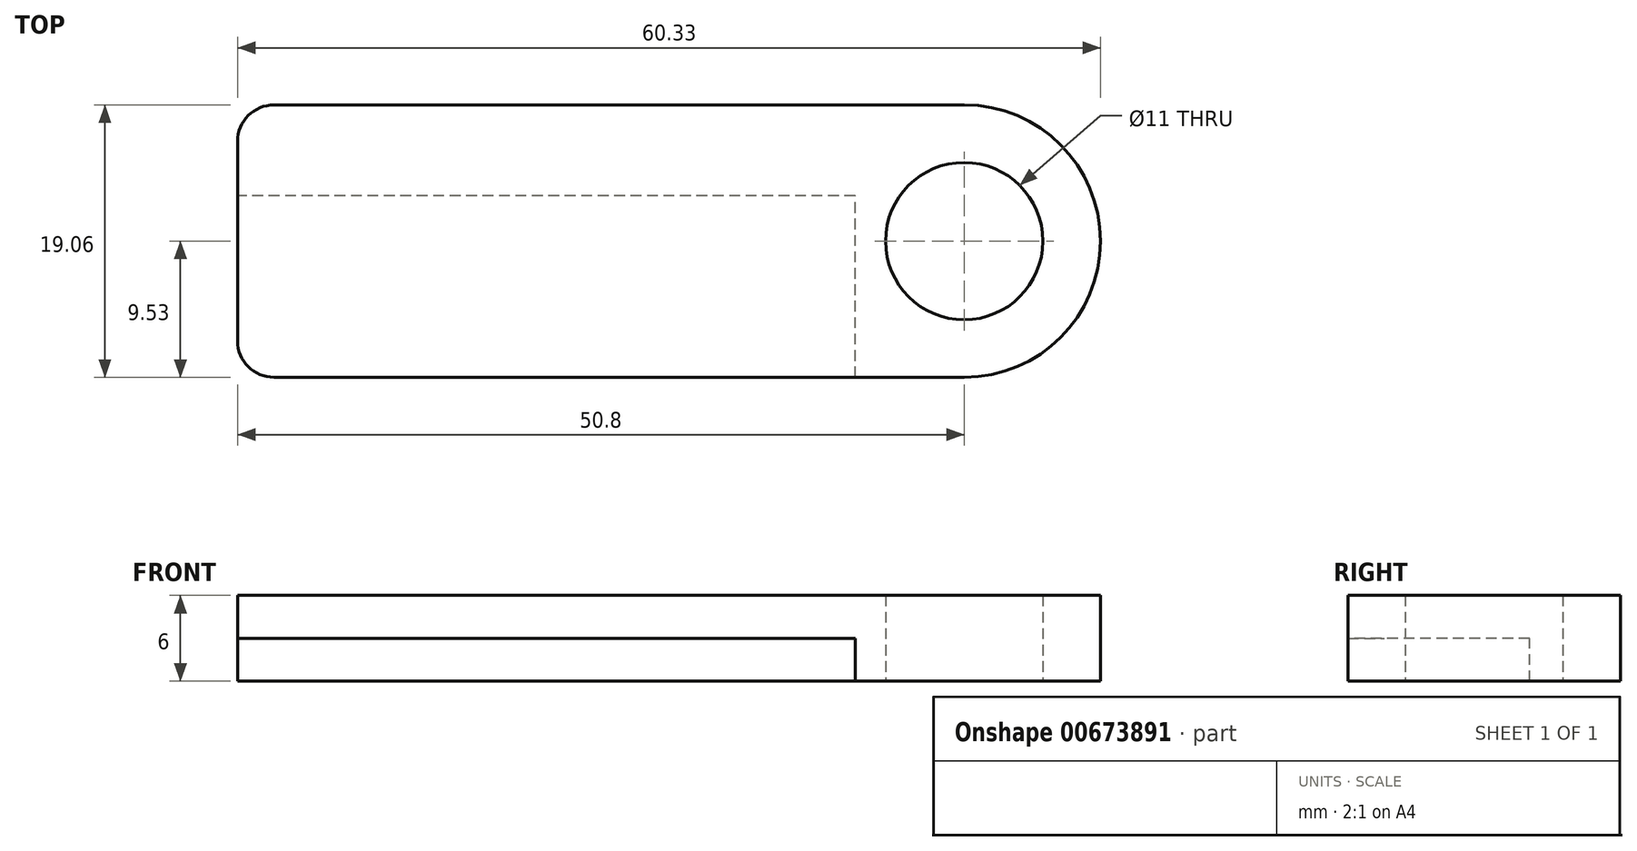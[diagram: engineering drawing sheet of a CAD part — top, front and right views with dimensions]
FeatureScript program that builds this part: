
annotation { "Feature Type Name" : "Feature", "Feature Type Description" : "" }
export const myFeature = defineFeature(function(context is Context, id is Id, definition is map)
    precondition{}
    {
        {
            var Q0;
            Q0=qCreatedBy(makeId("Top.planeOp"),FACE);
            var sketch = newSketch(context, id + "F0", { "sketchPlane" : qUnion([Q0])});
            skCircle(sketch, "E0", {"center": v(0, 0) * mm, "radius": 5.5 * mm});
            skArc(sketch, "E1", {"start": v(0, -9.53) * mm, "mid": v(9.53, 0) * mm, "end": v(0, 9.53) * mm});
            skLineSegment(sketch, "E2", {"start": v(0, 9.53) * mm, "end": v(-48.26, 9.53) * mm});
            skLineSegment(sketch, "E3", {"start": v(-50.8, 6.98) * mm, "end": v(-50.8, -6.98) * mm});
            skLineSegment(sketch, "E4", {"start": v(-48.26, -9.53) * mm, "end": v(0, -9.52) * mm});
            skArc(sketch, "E5", {"start": v(-48.26, 9.53) * mm, "mid": v(-50.06, 8.78) * mm, "end": v(-50.8, 6.98) * mm});
            skArc(sketch, "E6", {"start": v(-50.8, -6.98) * mm, "mid": v(-50.06, -8.78) * mm, "end": v(-48.26, -9.53) * mm});
            skSolve(sketch);
        }
        {
            var Q0;
            Q0=makeQuery(id+"F0.imprint","IMPRINT",FACE,{"disambiguationData":[TD([[makeQuery(id+"F0.imprint","IMPRINT",EDGE,{"derivedFrom":sQuery(id+"F0.wireOp",EDGE,"E0")}),-1.0]])]});
            extrude(context, id + "F1", {"entities" : qUnion([Q0]), "depth" : 6 * mm, "offsetDistance" : 25.4 * mm});
        }
        {
            var Q0;
            Q0=makeQuery(id+"F1.opExtrude","SWEPT_FACE",FACE,{"disambiguationData":[OSD([sQuery(id+"F0.wireOp",EDGE,"E3")])]});
            var sketch = newSketch(context, id + "F2", { "sketchPlane" : qUnion([Q0])});
            skLineSegment(sketch, "E7", {"start": v(9.53, 0) * mm, "end": v(-3.17, 0) * mm});
            skLineSegment(sketch, "E8", {"start": v(-3.17, 0) * mm, "end": v(-3.17, 3) * mm});
            skLineSegment(sketch, "E9", {"start": v(-3.17, 3) * mm, "end": v(9.53, 3) * mm});
            skLineSegment(sketch, "E10", {"start": v(9.53, 3) * mm, "end": v(9.53, 0) * mm});
            skPoint(sketch, "E11.orphan", {"position": v(9.53, 6) * mm});
            skSolve(sketch);
        }
        {
            var Q0;
            Q0 = qSketchRegion(id + "F2", true);
            extrude(context, id + "F3", {"entities" : qUnion([Q0]), "operationType" : NewBodyOperationType.REMOVE, "oppositeDirection" : true, "depth" : 43.18 * mm, "offsetDistance" : 25.4 * mm});
        }
    });
